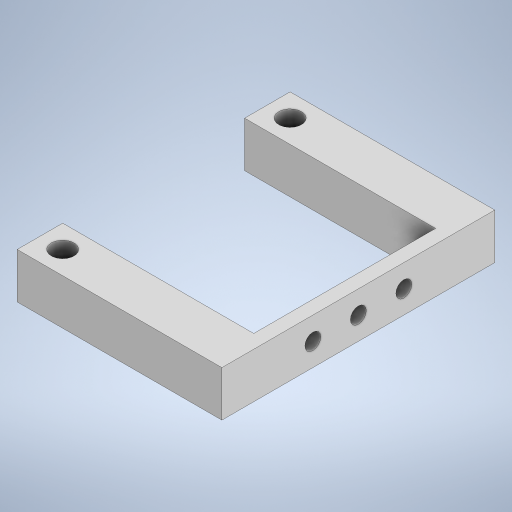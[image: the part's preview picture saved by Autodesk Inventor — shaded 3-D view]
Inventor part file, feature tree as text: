
AUTODESK INVENTOR PART (.ipt)
format: ipt  version: 2023 (Build 270158000, 158)  size: 253,952 bytes
history: native  units: mm
features: extrude x2, sketch x2, other x1
ambient origin geometry x8: Origin, YZ Plane, XZ Plane, XY Plane, X Axis, Y Axis, Z Axis, Center Point
bodies: Body1 (feature_tree)
feature tree (5):
  other  "Твердое тело1"
  extrude  "Выдавливание1"  Depth=90.0mm
  extrude  "Выдавливание2"  Depth=20.0mm
  sketch  "Эскиз1"
  sketch  "Эскиз2"
